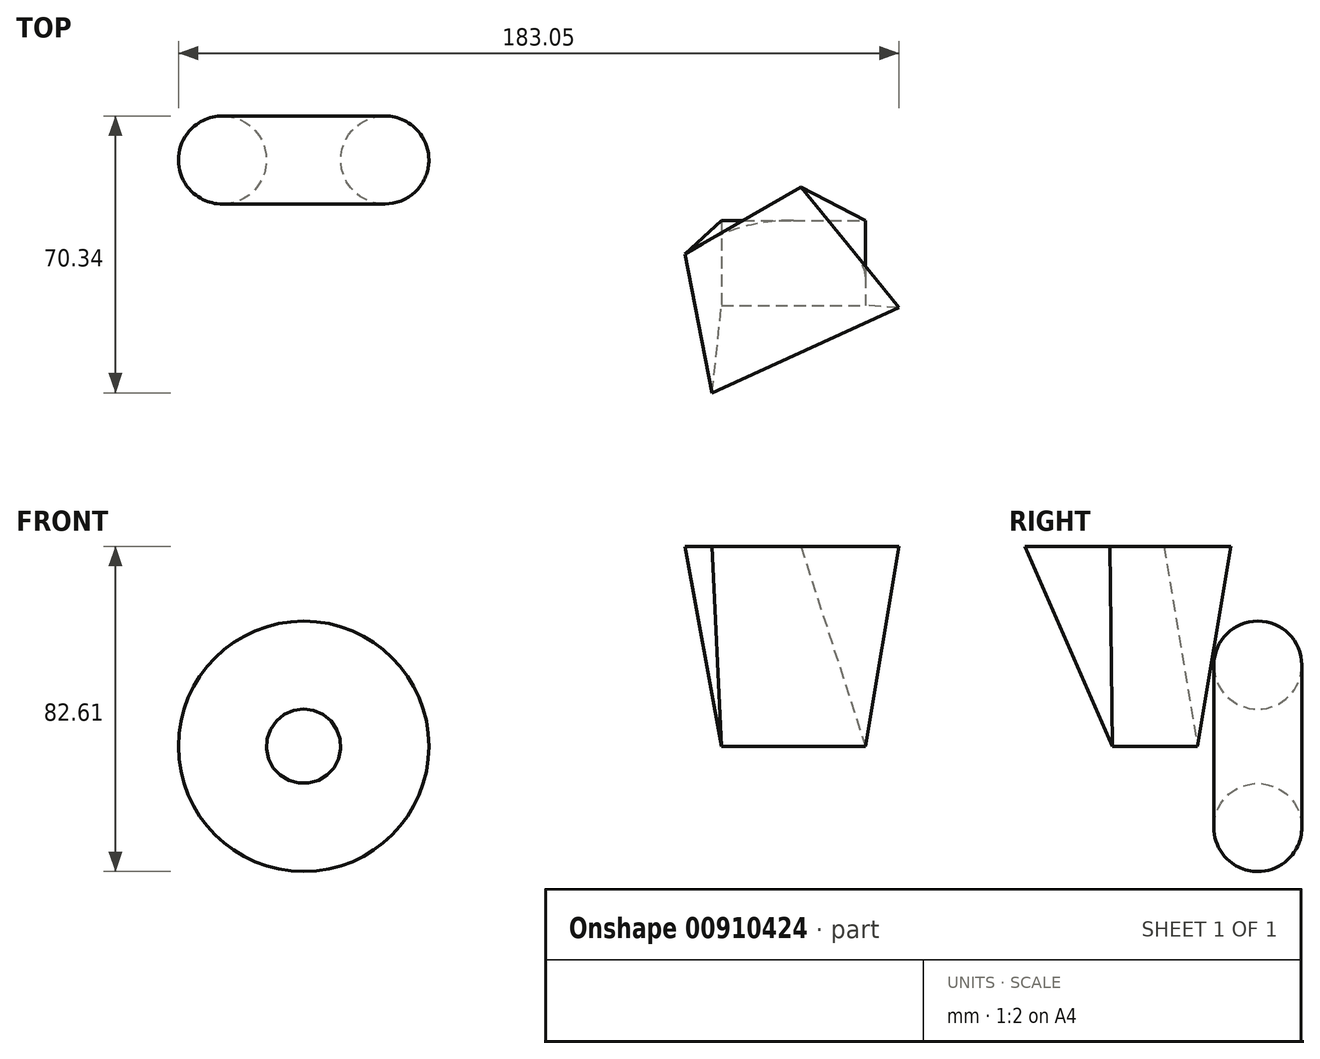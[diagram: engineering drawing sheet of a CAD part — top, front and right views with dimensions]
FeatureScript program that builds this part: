
annotation { "Feature Type Name" : "Feature", "Feature Type Description" : "" }
export const myFeature = defineFeature(function(context is Context, id is Id, definition is map)
    precondition{}
    {
        {
            var Q0;
            Q0=qCreatedBy(makeId("Top.planeOp"),FACE);
            var sketch = newSketch(context, id + "F0", { "sketchPlane" : qUnion([Q0])});
            skCircle(sketch, "E0", {"center": v(-62.28, 52.52) * mm, "radius": 11.18 * mm});
            skLineSegment(sketch, "E1.bottom", {"start": v(23.25, 37.16) * mm, "end": v(59.79, 37.16) * mm});
            skLineSegment(sketch, "E1.top", {"start": v(23.25, 15.57) * mm, "end": v(59.79, 15.57) * mm});
            skLineSegment(sketch, "E1.left", {"start": v(23.25, 37.16) * mm, "end": v(23.25, 15.57) * mm});
            skLineSegment(sketch, "E1.right", {"start": v(59.79, 37.16) * mm, "end": v(59.79, 15.57) * mm});
            skLineSegment(sketch, "E2", {"start": v(-55, -17.45) * mm, "end": v(-20.95, -29.08) * mm});
            skLineSegment(sketch, "E3", {"start": v(-20.95, -29.08) * mm, "end": v(-20.95, -63.13) * mm});
            skLineSegment(sketch, "E4", {"start": v(-20.95, -63.13) * mm, "end": v(-59.98, -69.35) * mm});
            skLineSegment(sketch, "E5", {"start": v(-59.98, -69.35) * mm, "end": v(-55, -17.45) * mm});
            skLineSegment(sketch, "E6", {"start": v(-82.91, 71.7) * mm, "end": v(-82.91, 30.26) * mm, "construction": true});
            skSolve(sketch);
        }
        {
            var Q0;
            Q0=qCreatedBy(makeId("Top.planeOp"),FACE);
            cPlane(context, id + "F1", {"entities" : qUnion([Q0]), "cplaneType" : CPlaneType.OFFSET, "offset" : 50.8 * mm, "width" : 152.4 * mm, "height" : 152.4 * mm});
        }
        {
            var Q0;
            Q0=qCreatedBy(id+"F1.planeOp",FACE);
            var sketch = newSketch(context, id + "F2", { "sketchPlane" : qUnion([Q0])});
            skCircle(sketch, "E7.0", {"center": v(-36.07, -47.94) * mm, "radius": 11.18 * mm});
            skLineSegment(sketch, "E7.1.0", {"start": v(-65.53, 33.82) * mm, "end": v(-46.83, 44.61) * mm});
            skLineSegment(sketch, "E7.1.1", {"start": v(-46.83, 44.61) * mm, "end": v(-65.1, 76.26) * mm});
            skLineSegment(sketch, "E7.1.2", {"start": v(-65.1, 76.26) * mm, "end": v(-83.8, 65.46) * mm});
            skLineSegment(sketch, "E7.1.3", {"start": v(-83.8, 65.46) * mm, "end": v(-65.53, 33.82) * mm});
            skLineSegment(sketch, "E7.2.0", {"start": v(20.9, -6.64) * mm, "end": v(68.33, 15) * mm});
            skLineSegment(sketch, "E7.2.1", {"start": v(68.33, 15) * mm, "end": v(43.42, 45.68) * mm});
            skLineSegment(sketch, "E7.2.2", {"start": v(43.42, 45.68) * mm, "end": v(13.94, 28.66) * mm});
            skLineSegment(sketch, "E7.2.3", {"start": v(13.94, 28.66) * mm, "end": v(20.9, -6.64) * mm});
            skSolve(sketch);
        }
        {
            var Q0;
            Q0=makeQuery(id+"F2.imprint","IMPRINT",FACE,{"disambiguationData":[TD([[makeQuery(id+"F2.imprint","IMPRINT",EDGE,{"derivedFrom":sQuery(id+"F2.wireOp",EDGE,"E7.2.0")}),1.0]])]});
            var Q1;
            Q1=makeQuery(id+"F0.imprint","IMPRINT",FACE,{"disambiguationData":[TD([[makeQuery(id+"F0.imprint","IMPRINT",EDGE,{"derivedFrom":sQuery(id+"F0.wireOp",EDGE,"E1.bottom")}),-1.0]])]});
            loft(context, id + "F3", {"sheetProfilesArray" : [{ "sheetProfileEntities" : qUnion([Q0]) }, { "sheetProfileEntities" : qUnion([Q1]) }]});
        }
        {
            var Q0;
            Q0=makeQuery(id+"F0.imprint","IMPRINT",FACE,{"disambiguationData":[TD([[makeQuery(id+"F0.imprint","IMPRINT",EDGE,{"derivedFrom":sQuery(id+"F0.wireOp",EDGE,"E0")}),1.0]])]});
            var Q1;
            Q1=sQuery(id+"F0.wireOp",EDGE,"E6");
            revolve(context, id + "F4", {"surfaceOperationType" : NewSurfaceOperationType.NEW, "entities" : qUnion([Q0]), "axis" : qUnion([Q1]), "revolveType" : RevolveType.FULL});
        }
    });
